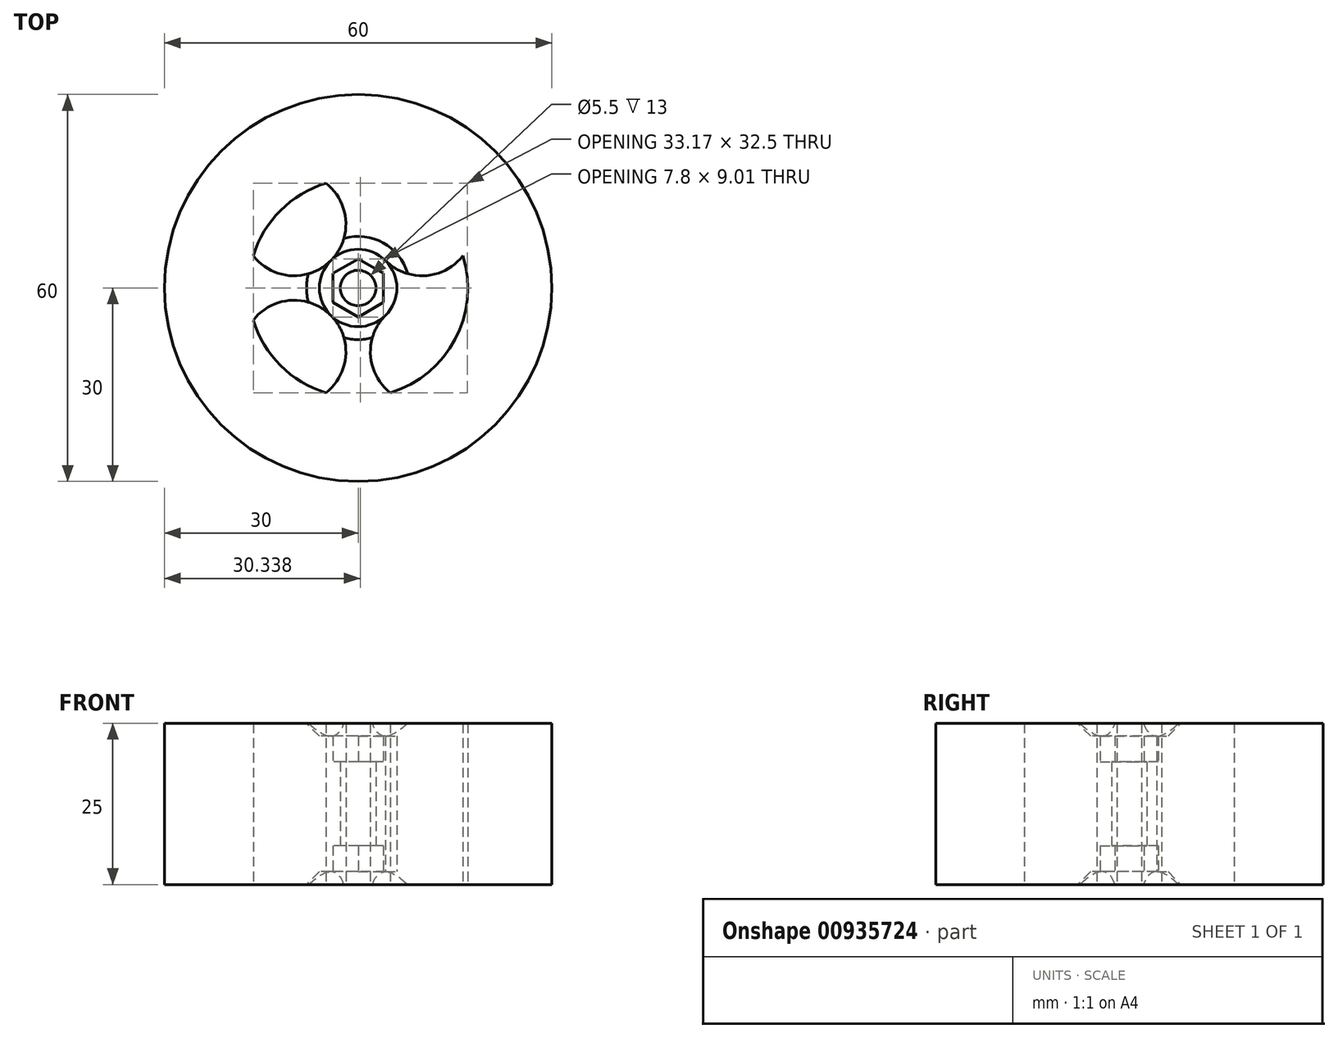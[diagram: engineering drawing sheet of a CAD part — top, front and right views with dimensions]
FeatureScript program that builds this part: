
annotation { "Feature Type Name" : "Feature", "Feature Type Description" : "" }
export const myFeature = defineFeature(function(context is Context, id is Id, definition is map)
    precondition{}
    {
        {
            var Q0;
            Q0=qCreatedBy(makeId("Top.planeOp"),FACE);
            var sketch = newSketch(context, id + "F0", { "sketchPlane" : qUnion([Q0])});
            skCircle(sketch, "E0", {"center": v(0, 0) * mm, "radius": 30 * mm});
            skCircle(sketch, "E1", {"center": v(0, 0) * mm, "radius": 17 * mm});
            skCircle(sketch, "E2", {"center": v(0, 0) * mm, "radius": 6 * mm});
            skArc(sketch, "E3", {"start": v(-16.25, 5) * mm, "mid": v(-4.24, 4.24) * mm, "end": v(-5, 16.25) * mm});
            skArc(sketch, "E4.MirrorCS", {"start": v(16.25, 5) * mm, "mid": v(4.24, 4.24) * mm, "end": v(5, 16.25) * mm});
            skArc(sketch, "E5.MirrorCS", {"start": v(16.25, -5) * mm, "mid": v(4.24, -4.24) * mm, "end": v(5, -16.25) * mm});
            skArc(sketch, "E6.MirrorCS", {"start": v(-16.25, -5) * mm, "mid": v(-4.24, -4.24) * mm, "end": v(-5, -16.25) * mm});
            skCircle(sketch, "E7.cCircle", {"center": v(0, 0) * mm, "radius": 3.9 * mm, "construction": true});
            skLineSegment(sketch, "E7.0", {"start": v(-3.9, -2.25) * mm, "end": v(-3.9, 2.25) * mm});
            skLineSegment(sketch, "E7.1", {"start": v(-3.9, 2.25) * mm, "end": v(0, 4.5) * mm});
            skLineSegment(sketch, "E7.2", {"start": v(0, 4.5) * mm, "end": v(3.9, 2.25) * mm});
            skLineSegment(sketch, "E7.3", {"start": v(3.9, 2.25) * mm, "end": v(3.9, -2.25) * mm});
            skLineSegment(sketch, "E7.4", {"start": v(3.9, -2.25) * mm, "end": v(0, -4.5) * mm});
            skLineSegment(sketch, "E7.5", {"start": v(0, -4.5) * mm, "end": v(-3.9, -2.25) * mm});
            skPoint(sketch, "E7.0.midPoint", {"position": v(-3.9, 0) * mm});
            skCircle(sketch, "E8", {"center": v(0, 0) * mm, "radius": 2.75 * mm});
            skCircle(sketch, "E9", {"center": v(0, 0) * mm, "radius": 3 * mm});
            skSolve(sketch);
        }
        {
            var Q0;
            {var subQ0=sQuery(id+"F0.wireOp",EDGE,"E4.MirrorCS");var subQ1=sQuery(id+"F0.wireOp",EDGE,"E1");var subQ2=makeQuery(id+"F0.imprint","INTERSECT",VERTEX,{"disambiguationData":[OD(0.0)],"derivedFrom":[subQ1,subQ0]});Q0=makeQuery(id+"F0.imprint","IMPRINT",FACE,{"disambiguationData":[TD([[makeQuery(id+"F0.imprint","IMPRINT",EDGE,{"disambiguationData":[TD([[subQ2,1.0]])],"derivedFrom":subQ1}),1.0]])]});}
            var Q1;
            {var subQ0=sQuery(id+"F0.wireOp",EDGE,"E3");var subQ1=sQuery(id+"F0.wireOp",EDGE,"E1");var subQ2=makeQuery(id+"F0.imprint","INTERSECT",VERTEX,{"disambiguationData":[OD(1.0)],"derivedFrom":[subQ1,subQ0]});Q1=makeQuery(id+"F0.imprint","IMPRINT",FACE,{"disambiguationData":[TD([[makeQuery(id+"F0.imprint","IMPRINT",EDGE,{"disambiguationData":[TD([[subQ2,1.0]])],"derivedFrom":subQ1}),1.0]])]});}
            var Q2;
            {var subQ0=sQuery(id+"F0.wireOp",EDGE,"E2");var subQ1=makeQuery(id+"F0.imprint","INTERSECT",VERTEX,{"derivedFrom":[subQ0,sQuery(id+"F0.wireOp",EDGE,"E3")]});Q2=makeQuery(id+"F0.imprint","IMPRINT",FACE,{"disambiguationData":[TD([[makeQuery(id+"F0.imprint","IMPRINT",EDGE,{"disambiguationData":[TD([[subQ1,1.0]])],"derivedFrom":subQ0}),1.0]])]});}
            var Q3;
            {var subQ0=sQuery(id+"F0.wireOp",EDGE,"E5.MirrorCS");var subQ1=sQuery(id+"F0.wireOp",EDGE,"E1");var subQ2=makeQuery(id+"F0.imprint","INTERSECT",VERTEX,{"disambiguationData":[OD(1.0)],"derivedFrom":[subQ1,subQ0]});Q3=makeQuery(id+"F0.imprint","IMPRINT",FACE,{"disambiguationData":[TD([[makeQuery(id+"F0.imprint","IMPRINT",EDGE,{"disambiguationData":[TD([[subQ2,1.0]])],"derivedFrom":subQ1}),1.0]])]});}
            var Q4;
            {var subQ0=sQuery(id+"F0.wireOp",EDGE,"E3");var subQ1=sQuery(id+"F0.wireOp",EDGE,"E1");var subQ2=makeQuery(id+"F0.imprint","INTERSECT",VERTEX,{"disambiguationData":[OD(0.0)],"derivedFrom":[subQ1,subQ0]});Q4=makeQuery(id+"F0.imprint","IMPRINT",FACE,{"disambiguationData":[TD([[makeQuery(id+"F0.imprint","IMPRINT",EDGE,{"disambiguationData":[TD([[subQ2,-1.0]])],"derivedFrom":subQ1}),1.0]])]});}
            var Q5;
            Q5=makeQuery(id+"F0.imprint","IMPRINT",FACE,{"disambiguationData":[TD([[makeQuery(id+"F0.imprint","IMPRINT",EDGE,{"derivedFrom":sQuery(id+"F0.wireOp",EDGE,"AWBVtN4J-C4oJ-jGMu-giAT-Llfum83dGoXK")}),1.0]])]});
            var Q6;
            Q6=makeQuery(id+"F0.imprint","IMPRINT",FACE,{"disambiguationData":[TD([[makeQuery(id+"F0.imprint","IMPRINT",EDGE,{"derivedFrom":sQuery(id+"F0.wireOp",EDGE,"nk7Qsrv0-wqnY-I9nE-Y8dC-PY7UgDYU0npt")}),1.0]])]});
            var Q7;
            Q7=makeQuery(id+"F0.imprint","IMPRINT",FACE,{"disambiguationData":[TD([[makeQuery(id+"F0.imprint","IMPRINT",EDGE,{"derivedFrom":sQuery(id+"F0.wireOp",EDGE,"E7.0")}),-1.0]])]});
            var Q8;
            Q8=makeQuery(id+"F0.imprint","IMPRINT",FACE,{"disambiguationData":[TD([[makeQuery(id+"F0.imprint","IMPRINT",EDGE,{"derivedFrom":sQuery(id+"F0.wireOp",EDGE,"E0")}),1.0]])]});
            extrude(context, id + "F1", {"entities" : qUnion([Q0, Q1, Q2, Q3, Q4, Q5, Q6, Q7, Q8]), "depth" : 25 * mm, "offsetDistance" : 25 * mm});
        }
        {
            var Q0;
            Q0=makeQuery(id+"F0.imprint","IMPRINT",FACE,{"disambiguationData":[TD([[makeQuery(id+"F0.imprint","IMPRINT",EDGE,{"derivedFrom":sQuery(id+"F0.wireOp",EDGE,"E8")}),-1.0]])]});
            extrude(context, id + "F2", {"entities" : qUnion([Q0]), "operationType" : NewBodyOperationType.ADD, "depth" : 23 * mm, "offsetDistance" : 25 * mm, "hasSecondDirection" : true, "secondDirectionOppositeDirection" : false, "secondDirectionDepth" : 2 * mm});
        }
        {
            var Q0;
            Q0=makeQuery(id+"F1.opExtrude","CAP_EDGE",EDGE,{"disambiguationData":[OSD([sQuery(id+"F0.wireOp",EDGE,"E9")])],"isStart":true});
            var Q1;
            Q1=makeQuery(id+"F1.opExtrude","CAP_EDGE",EDGE,{"disambiguationData":[OSD([sQuery(id+"F0.wireOp",EDGE,"E9")])],"isStart":false});
            chamfer(context, id + "F3", {"entities" : qUnion([Q0, Q1]), "width" : 5 * mm, "tangentPropagation" : true});
        }
        {
            var Q0;
            Q0=makeQuery(id+"F0.imprint","IMPRINT",FACE,{"disambiguationData":[TD([[makeQuery(id+"F0.imprint","IMPRINT",EDGE,{"derivedFrom":sQuery(id+"F0.wireOp",EDGE,"E7.0")}),-1.0]])]});
            var Q1;
            Q1=makeQuery(id+"F0.imprint","IMPRINT",FACE,{"disambiguationData":[TD([[makeQuery(id+"F0.imprint","IMPRINT",EDGE,{"derivedFrom":sQuery(id+"F0.wireOp",EDGE,"E8")}),1.0]])]});
            var Q2;
            Q2=makeQuery(id+"F0.imprint","IMPRINT",FACE,{"disambiguationData":[TD([[makeQuery(id+"F0.imprint","IMPRINT",EDGE,{"derivedFrom":sQuery(id+"F0.wireOp",EDGE,"E8")}),-1.0]])]});
            extrude(context, id + "F4", {"entities" : qUnion([Q0, Q1, Q2]), "operationType" : NewBodyOperationType.REMOVE, "depth" : 6 * mm, "offsetDistance" : 25 * mm});
        }
        {
            var Q0;
            Q0=makeQuery(id+"F0.imprint","IMPRINT",FACE,{"disambiguationData":[TD([[makeQuery(id+"F0.imprint","IMPRINT",EDGE,{"derivedFrom":sQuery(id+"F0.wireOp",EDGE,"E7.0")}),-1.0]])]});
            var Q1;
            Q1=makeQuery(id+"F0.imprint","IMPRINT",FACE,{"disambiguationData":[TD([[makeQuery(id+"F0.imprint","IMPRINT",EDGE,{"derivedFrom":sQuery(id+"F0.wireOp",EDGE,"E8")}),-1.0]])]});
            var Q2;
            Q2=makeQuery(id+"F2.opExtrude","CAP_FACE",FACE,{"disambiguationData":[OSD([sQuery(id+"F0.wireOp",EDGE,"E8"),sQuery(id+"F0.wireOp",EDGE,"E9")])],"isStart":false});
            extrude(context, id + "F5", {"entities" : qUnion([Q0, Q1]), "operationType" : NewBodyOperationType.REMOVE, "endBound" : BoundingType.UP_TO_SURFACE, "depth" : 25 * mm, "endBoundEntityFace" : qUnion([Q2]), "offsetDistance" : 25 * mm, "hasSecondDirection" : true, "secondDirectionOppositeDirection" : false, "secondDirectionDepth" : 19 * mm});
        }
    });
